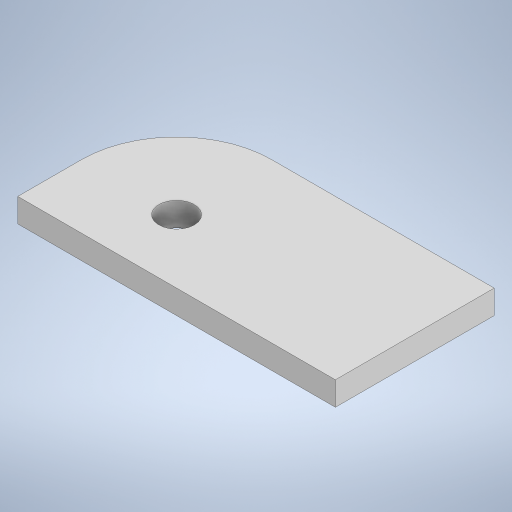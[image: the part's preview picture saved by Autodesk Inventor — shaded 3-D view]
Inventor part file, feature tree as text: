
AUTODESK INVENTOR PART (.ipt)
format: ipt  version: 2024 (Build 280153000, 153)  size: 213,504 bytes
history: native  units: mm
features: extrude x2, sketch x2, fillet x1
ambient origin geometry x8: Origin, YZ Plane, XZ Plane, XY Plane, X Axis, Y Axis, Z Axis, Center Point
bodies: Solid1 (feature_tree)
feature tree (5):
  extrude  "Extrusion1"  Depth=200.0mm
  fillet  "Fillet2"  Radius=15.0mm
  extrude  "Extrusion2"  Depth=15.0mm TaperAngle=0.0deg
  sketch  "Sketch1"  dims[d0=100.0mm d1=200.0mm d2=15.0mm d3=0.0mm]
  sketch  "Sketch2"  dims[d5=60.0mm d6=15.0mm d7=0.0mm]
